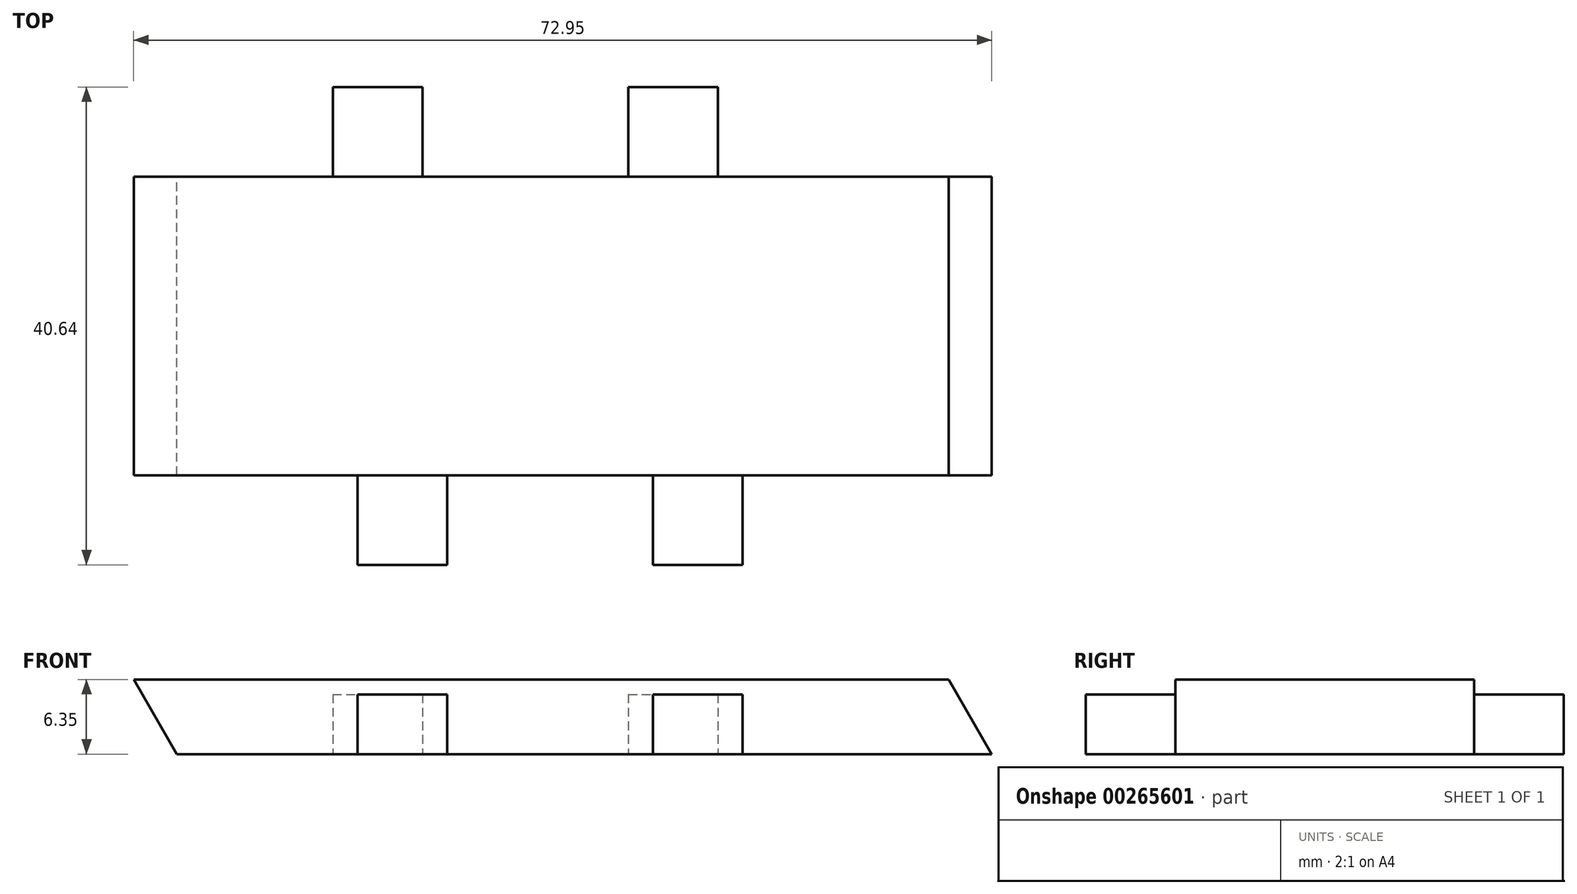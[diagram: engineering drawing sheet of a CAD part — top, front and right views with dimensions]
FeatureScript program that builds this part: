
annotation { "Feature Type Name" : "Feature", "Feature Type Description" : "" }
export const myFeature = defineFeature(function(context is Context, id is Id, definition is map)
    precondition{}
    {
        {
            var Q0;
            Q0=qCreatedBy(makeId("Top.planeOp"),FACE);
            var sketch = newSketch(context, id + "F0", { "sketchPlane" : qUnion([Q0])});
            skLineSegment(sketch, "E0.bottom", {"start": v(-41.25, -7.62) * mm, "end": v(32.84, -7.62) * mm});
            skLineSegment(sketch, "E0.top", {"start": v(-41.25, -33.02) * mm, "end": v(32.84, -33.02) * mm});
            skLineSegment(sketch, "E0.left", {"start": v(-41.25, -7.62) * mm, "end": v(-41.25, -33.02) * mm});
            skLineSegment(sketch, "E0.right", {"start": v(32.84, -7.62) * mm, "end": v(32.84, -33.02) * mm});
            skLineSegment(sketch, "E1", {"start": v(-41.25, -7.62) * mm, "end": v(-41.25, 18.72) * mm, "construction": true});
            skLineSegment(sketch, "E2", {"start": v(32.84, -7.62) * mm, "end": v(32.84, 15.65) * mm, "construction": true});
            skLineSegment(sketch, "E3", {"start": v(-41.25, -33.02) * mm, "end": v(-41.25, -58.09) * mm, "construction": true});
            skLineSegment(sketch, "E4", {"start": v(32.84, -33.02) * mm, "end": v(32.84, -60.63) * mm, "construction": true});
            skLineSegment(sketch, "E5", {"start": v(-23.75, -7.62) * mm, "end": v(-23.75, 0) * mm});
            skLineSegment(sketch, "E6", {"start": v(-23.75, 0) * mm, "end": v(-16.13, 0) * mm});
            skLineSegment(sketch, "E7", {"start": v(-16.13, 0) * mm, "end": v(-16.13, -7.62) * mm});
            skLineSegment(sketch, "E8", {"start": v(1.37, -7.62) * mm, "end": v(1.37, 0) * mm});
            skLineSegment(sketch, "E9", {"start": v(1.37, 0) * mm, "end": v(9, 0) * mm});
            skLineSegment(sketch, "E10", {"start": v(9, 0) * mm, "end": v(9, -7.62) * mm});
            skLineSegment(sketch, "E11", {"start": v(-21.64, -33.02) * mm, "end": v(-21.64, -40.64) * mm});
            skLineSegment(sketch, "E12", {"start": v(-21.64, -40.64) * mm, "end": v(-14.02, -40.64) * mm});
            skLineSegment(sketch, "E13", {"start": v(-14.02, -40.64) * mm, "end": v(-14.02, -33.02) * mm});
            skLineSegment(sketch, "E14", {"start": v(3.48, -33.02) * mm, "end": v(3.48, -40.64) * mm});
            skLineSegment(sketch, "E15", {"start": v(3.48, -40.64) * mm, "end": v(11.1, -40.64) * mm});
            skLineSegment(sketch, "E16", {"start": v(11.1, -40.64) * mm, "end": v(11.1, -33.02) * mm});
            skSolve(sketch);
        }
        {
            var Q0;
            {var subQ0=sQuery(id+"F0.wireOp",EDGE,"E0.left");Q0=makeQuery(id+"F0.imprint","IMPRINT",FACE,{"disambiguationData":[TD([[makeQuery(id+"F0.imprint","IMPRINT",EDGE,{"derivedFrom":subQ0}),1.0]])]});}
            extrude(context, id + "F1", {"entities" : qUnion([Q0]), "depth" : 6.35 * mm});
        }
        {
            var Q0;
            {var subQ0=sQuery(id+"F0.wireOp",EDGE,"E5");Q0=makeQuery(id+"F0.imprint","IMPRINT",FACE,{"disambiguationData":[TD([[makeQuery(id+"F0.imprint","IMPRINT",EDGE,{"derivedFrom":subQ0}),-1.0]])]});}
            var Q1;
            {var subQ0=sQuery(id+"F0.wireOp",EDGE,"E11");Q1=makeQuery(id+"F0.imprint","IMPRINT",FACE,{"disambiguationData":[TD([[makeQuery(id+"F0.imprint","IMPRINT",EDGE,{"derivedFrom":subQ0}),1.0]])]});}
            var Q2;
            {var subQ0=sQuery(id+"F0.wireOp",EDGE,"E14");Q2=makeQuery(id+"F0.imprint","IMPRINT",FACE,{"disambiguationData":[TD([[makeQuery(id+"F0.imprint","IMPRINT",EDGE,{"derivedFrom":subQ0}),1.0]])]});}
            var Q3;
            {var subQ0=sQuery(id+"F0.wireOp",EDGE,"E8");Q3=makeQuery(id+"F0.imprint","IMPRINT",FACE,{"disambiguationData":[TD([[makeQuery(id+"F0.imprint","IMPRINT",EDGE,{"derivedFrom":subQ0}),-1.0]])]});}
            extrude(context, id + "F2", {"entities" : qUnion([Q0, Q1, Q2, Q3]), "operationType" : NewBodyOperationType.ADD, "depth" : 5.08 * mm});
        }
        {
            var Q0;
            Q0=makeQuery(id+"F1.opExtrude","CAP_EDGE",EDGE,{"disambiguationData":[OSD([sQuery(id+"F0.wireOp",EDGE,"E0.right")])],"isStart":false});
            var Q1;
            Q1=makeQuery(id+"F1.opExtrude","CAP_EDGE",EDGE,{"disambiguationData":[OSD([sQuery(id+"F0.wireOp",EDGE,"E0.left")])],"isStart":true});
            chamfer(context, id + "F3", {"entities" : qUnion([Q0, Q1]), "chamferType" : ChamferType.OFFSET_ANGLE, "width" : 7.34 * mm, "oppositeDirection" : false, "angle" : 30 * degree, "tangentPropagation" : true});
        }
    });
